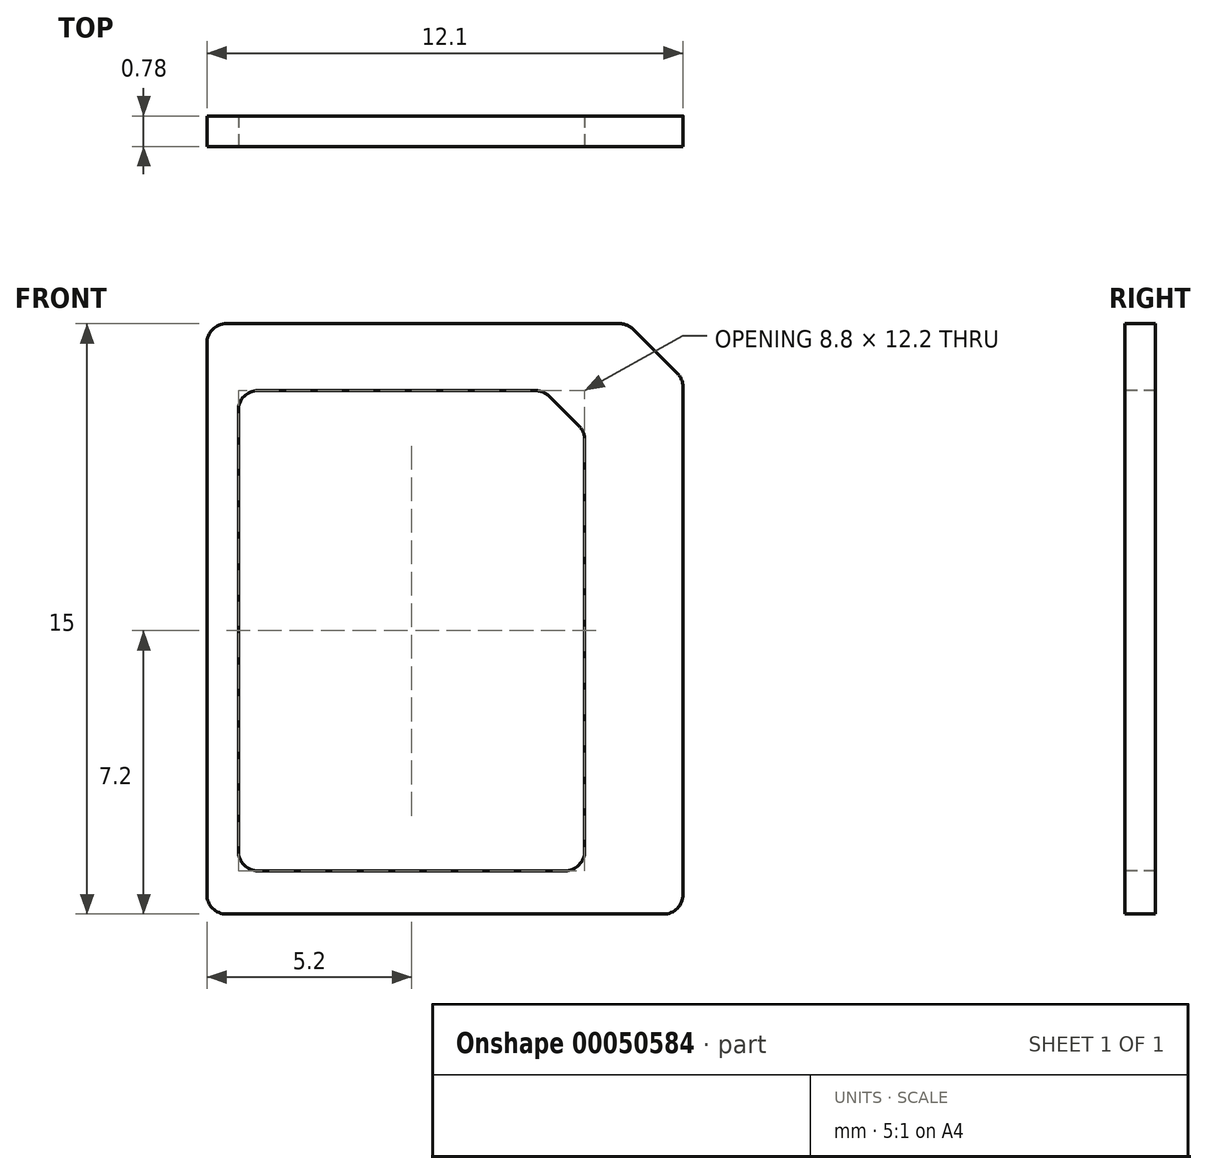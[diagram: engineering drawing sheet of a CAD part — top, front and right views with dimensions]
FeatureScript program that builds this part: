
annotation { "Feature Type Name" : "Feature", "Feature Type Description" : "" }
export const myFeature = defineFeature(function(context is Context, id is Id, definition is map)
    precondition{}
    {
        {
            var Q0;
            Q0=qCreatedBy(makeId("Front.planeOp"),FACE);
            var sketch = newSketch(context, id + "F0", { "sketchPlane" : qUnion([Q0])});
            skLineSegment(sketch, "E0.rect.bottom", {"start": v(-6.05, 7.5) * mm, "end": v(4.64, 7.5) * mm});
            skLineSegment(sketch, "E0.rect.top", {"start": v(-6.05, -7.5) * mm, "end": v(6.05, -7.5) * mm});
            skLineSegment(sketch, "E0.rect.left", {"start": v(-6.05, 7.5) * mm, "end": v(-6.05, -7.5) * mm});
            skLineSegment(sketch, "E0.rect.right", {"start": v(6.05, 6.09) * mm, "end": v(6.05, -7.5) * mm});
            skPoint(sketch, "E0.rect.middle", {"position": v(0, 0) * mm});
            skLineSegment(sketch, "E1", {"start": v(4.64, 7.5) * mm, "end": v(6.05, 6.09) * mm});
            skPoint(sketch, "E2.orphan", {"position": v(6.05, 7.5) * mm});
            skSolve(sketch);
        }
        {
            var Q0;
            Q0=makeQuery(id+"F0.imprint","IMPRINT",FACE,{"disambiguationData":[TD([[makeQuery(id+"F0.imprint","IMPRINT",EDGE,{"derivedFrom":sQuery(id+"F0.wireOp",EDGE,"E0.rect.bottom")}),-1.0]])]});
            extrude(context, id + "F1", {"entities" : qUnion([Q0]), "depth" : 0.78 * mm});
        }
        {
            var Q0;
            Q0=makeQuery(id+"F1.opExtrude","SWEPT_EDGE",EDGE,{"disambiguationData":[OSD([sQuery(id+"F0.wireOp",EDGE,"E0.rect.bottom"),sQuery(id+"F0.wireOp",EDGE,"E0.rect.left")])]});
            var Q1;
            Q1=makeQuery(id+"F1.opExtrude","SWEPT_EDGE",EDGE,{"disambiguationData":[OSD([sQuery(id+"F0.wireOp",EDGE,"E0.rect.top"),sQuery(id+"F0.wireOp",EDGE,"E0.rect.left")])]});
            var Q2;
            Q2=makeQuery(id+"F1.opExtrude","SWEPT_EDGE",EDGE,{"disambiguationData":[OSD([sQuery(id+"F0.wireOp",EDGE,"E0.rect.top"),sQuery(id+"F0.wireOp",EDGE,"E0.rect.right")])]});
            var Q3;
            Q3=makeQuery(id+"F1.opExtrude","SWEPT_EDGE",EDGE,{"disambiguationData":[OSD([sQuery(id+"F0.wireOp",EDGE,"E0.rect.bottom"),sQuery(id+"F0.wireOp",EDGE,"E0.rect.right")])]});
            fillet(context, id + "F2", {"entities" : qUnion([Q0, Q1, Q2, Q3]), "radius" : 0.5 * mm, "tangentPropagation" : true, "allowEdgeOverflow" : false});
        }
        {
            var Q0;
            Q0=makeQuery(id+"F1.opExtrude","CAP_FACE",FACE,{"disambiguationData":[OSD([sQuery(id+"F0.wireOp",EDGE,"E0.rect.bottom"),sQuery(id+"F0.wireOp",EDGE,"E0.rect.top"),sQuery(id+"F0.wireOp",EDGE,"E0.rect.left"),sQuery(id+"F0.wireOp",EDGE,"E0.rect.right")])],"isStart":false});
            var sketch = newSketch(context, id + "F3", { "sketchPlane" : qUnion([Q0])});
            skLineSegment(sketch, "E3.bottom", {"start": v(-5.25, 5.8) * mm, "end": v(2.5, 5.8) * mm});
            skLineSegment(sketch, "E3.top", {"start": v(-5.25, -6.4) * mm, "end": v(3.55, -6.4) * mm});
            skLineSegment(sketch, "E3.left", {"start": v(-5.25, 5.8) * mm, "end": v(-5.25, -6.4) * mm});
            skLineSegment(sketch, "E3.right", {"start": v(3.55, 4.76) * mm, "end": v(3.55, -6.4) * mm});
            skLineSegment(sketch, "E4", {"start": v(2.5, 5.8) * mm, "end": v(3.55, 4.76) * mm});
            skLineSegment(sketch, "E5", {"start": v(-1.37, 5.8) * mm, "end": v(-1.37, 7.5) * mm, "construction": true});
            skSolve(sketch);
        }
        {
            var Q0;
            Q0=makeQuery(id+"F3.imprint","IMPRINT",FACE,{"disambiguationData":[TD([[makeQuery(id+"F3.imprint","IMPRINT",EDGE,{"derivedFrom":sQuery(id+"F3.wireOp",EDGE,"E3.bottom")}),-1.0]])]});
            extrude(context, id + "F4", {"entities" : qUnion([Q0]), "operationType" : NewBodyOperationType.REMOVE, "oppositeDirection" : true, "depth" : 25 * mm});
        }
        {
            var Q0;
            Q0=makeQuery(id+"F4.boolean.opBoolean","COPY",EDGE,{"derivedFrom":makeQuery(id+"F4.opExtrude","SWEPT_EDGE",EDGE,{"disambiguationData":[OSD([sQuery(id+"F3.wireOp",EDGE,"E3.bottom"),sQuery(id+"F3.wireOp",EDGE,"E3.left")])]})});
            var Q1;
            Q1=makeQuery(id+"F4.boolean.opBoolean","COPY",EDGE,{"derivedFrom":makeQuery(id+"F4.opExtrude","SWEPT_EDGE",EDGE,{"disambiguationData":[OSD([sQuery(id+"F3.wireOp",EDGE,"E3.top"),sQuery(id+"F3.wireOp",EDGE,"E3.left")])]})});
            var Q2;
            Q2=makeQuery(id+"F4.boolean.opBoolean","COPY",EDGE,{"derivedFrom":makeQuery(id+"F4.opExtrude","SWEPT_EDGE",EDGE,{"disambiguationData":[OSD([sQuery(id+"F3.wireOp",EDGE,"E3.top"),sQuery(id+"F3.wireOp",EDGE,"E3.right")])]})});
            var Q3;
            Q3=makeQuery(id+"F4.boolean.opBoolean","COPY",EDGE,{"derivedFrom":makeQuery(id+"F4.opExtrude","SWEPT_EDGE",EDGE,{"disambiguationData":[OSD([sQuery(id+"F3.wireOp",EDGE,"E3.bottom"),sQuery(id+"F3.wireOp",EDGE,"E3.right")])]})});
            fillet(context, id + "F5", {"entities" : qUnion([Q0, Q1, Q2, Q3]), "radius" : 0.5 * mm, "tangentPropagation" : true, "allowEdgeOverflow" : false});
        }
    });
